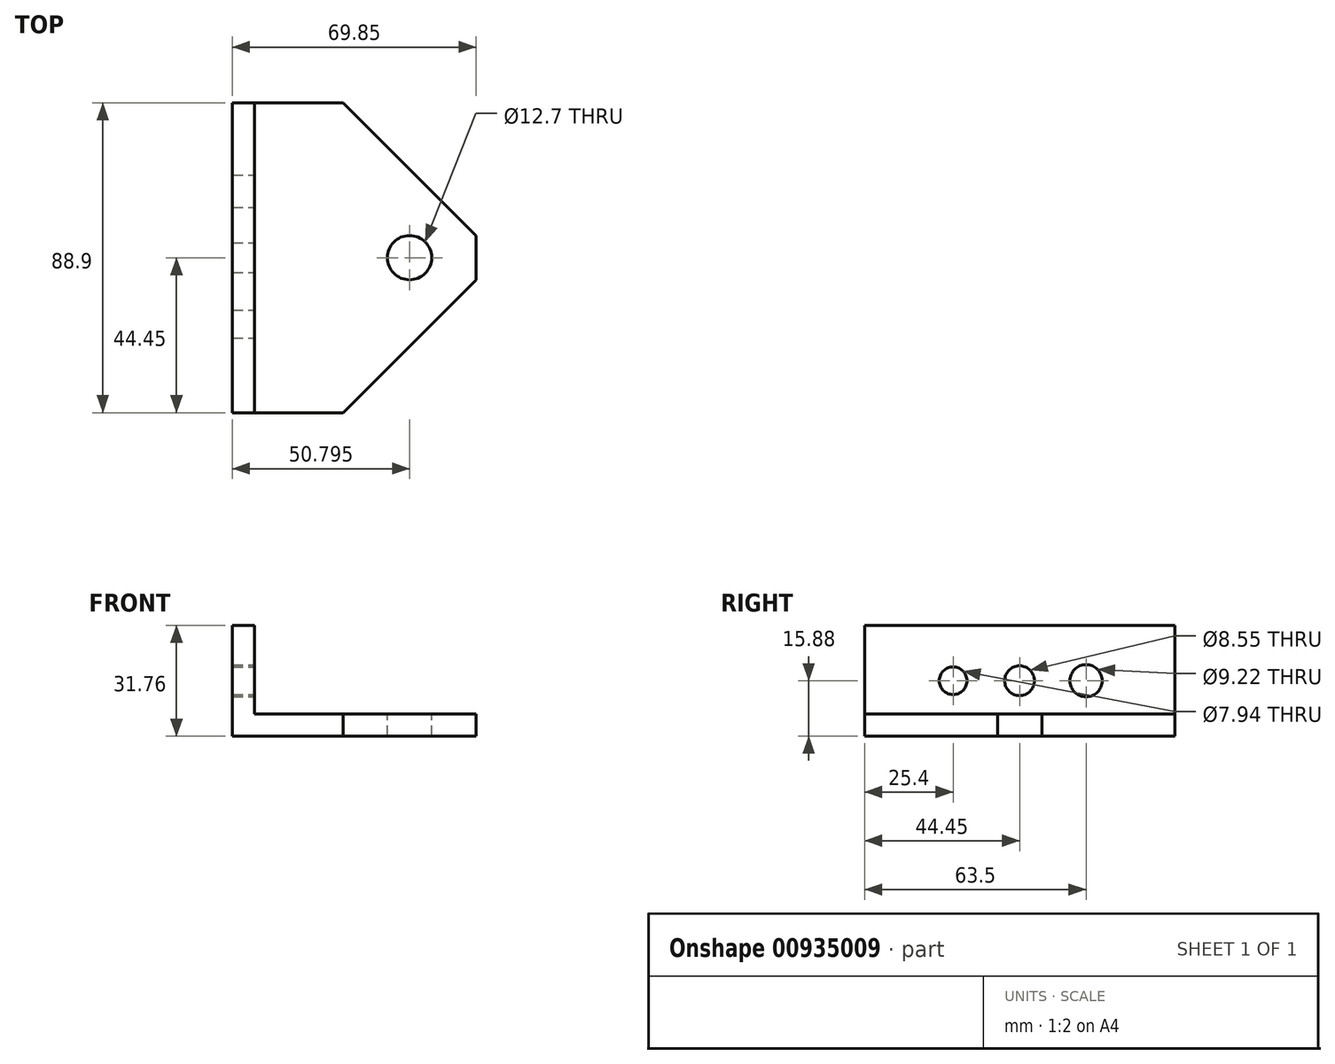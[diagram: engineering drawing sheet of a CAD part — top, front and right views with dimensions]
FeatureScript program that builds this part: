
annotation { "Feature Type Name" : "Feature", "Feature Type Description" : "" }
export const myFeature = defineFeature(function(context is Context, id is Id, definition is map)
    precondition{}
    {
        {
            var Q0;
            Q0=qCreatedBy(makeId("Front.planeOp"),FACE);
            var sketch = newSketch(context, id + "F0", { "sketchPlane" : qUnion([Q0])});
            skLineSegment(sketch, "E0.bottom", {"start": v(-4.48, 15.88) * mm, "end": v(1.87, 15.88) * mm});
            skLineSegment(sketch, "E0.top", {"start": v(-4.48, -15.88) * mm, "end": v(1.87, -15.88) * mm});
            skLineSegment(sketch, "E0.left", {"start": v(-4.48, 15.88) * mm, "end": v(-4.48, -15.88) * mm});
            skLineSegment(sketch, "E0.right", {"start": v(1.87, 15.88) * mm, "end": v(1.87, -15.88) * mm});
            skPoint(sketch, "E0.middle", {"position": v(-1.3, 0) * mm});
            skLineSegment(sketch, "E1.bottom", {"start": v(1.87, -15.88) * mm, "end": v(65.37, -15.87) * mm});
            skLineSegment(sketch, "E1.top", {"start": v(1.87, -9.52) * mm, "end": v(65.37, -9.52) * mm});
            skLineSegment(sketch, "E1.left", {"start": v(1.87, -15.88) * mm, "end": v(1.87, -9.52) * mm});
            skLineSegment(sketch, "E1.right", {"start": v(65.37, -15.87) * mm, "end": v(65.37, -9.52) * mm});
            skSolve(sketch);
        }
        {
            var Q0;
            Q0 = qSketchRegion(id + "F0", true);
            extrude(context, id + "F1", {"entities" : qUnion([Q0]), "depth" : 88.9 * mm, "offsetDistance" : 25.4 * mm, "symmetric" : true});
        }
        {
            var Q0;
            Q0=makeQuery(id+"F1.opExtrude","CAP_EDGE",EDGE,{"disambiguationData":[OSD([sQuery(id+"F0.wireOp",EDGE,"E1.right")])],"isStart":true});
            chamfer(context, id + "F2", {"entities" : qUnion([Q0]), "width" : 38.1 * mm, "tangentPropagation" : true});
        }
        {
            var Q0;
            Q0=makeQuery(id+"F1.opExtrude","CAP_EDGE",EDGE,{"disambiguationData":[OSD([sQuery(id+"F0.wireOp",EDGE,"E1.right")])],"isStart":false});
            chamfer(context, id + "F3", {"entities" : qUnion([Q0]), "width" : 38.1 * mm, "tangentPropagation" : true});
        }
        {
            var Q0;
            Q0=qCreatedBy(makeId("Right.planeOp"),FACE);
            var sketch = newSketch(context, id + "F4", { "sketchPlane" : qUnion([Q0])});
            skCircle(sketch, "E2", {"center": v(0, 0) * mm, "radius": 4.27 * mm});
            skCircle(sketch, "E3", {"center": v(19.05, 0) * mm, "radius": 4.61 * mm});
            skCircle(sketch, "E4", {"center": v(-19.05, 0) * mm, "radius": 3.97 * mm});
            skSolve(sketch);
        }
        {
            var Q0;
            Q0 = qSketchRegion(id + "F4", true);
            extrude(context, id + "F5", {"entities" : qUnion([Q0]), "operationType" : NewBodyOperationType.REMOVE, "oppositeDirection" : true, "depth" : 254 * mm, "offsetDistance" : 25.4 * mm, "symmetric" : true});
        }
        {
            var Q0;
            Q0=qCreatedBy(makeId("Top.planeOp"),FACE);
            var sketch = newSketch(context, id + "F6", { "sketchPlane" : qUnion([Q0])});
            skCircle(sketch, "E5", {"center": v(46.32, 0) * mm, "radius": 6.35 * mm});
            skSolve(sketch);
        }
        {
            var Q0;
            Q0 = qSketchRegion(id + "F6", true);
            extrude(context, id + "F7", {"entities" : qUnion([Q0]), "operationType" : NewBodyOperationType.REMOVE, "oppositeDirection" : true, "depth" : 254 * mm, "offsetDistance" : 25.4 * mm, "symmetric" : true});
        }
    });
